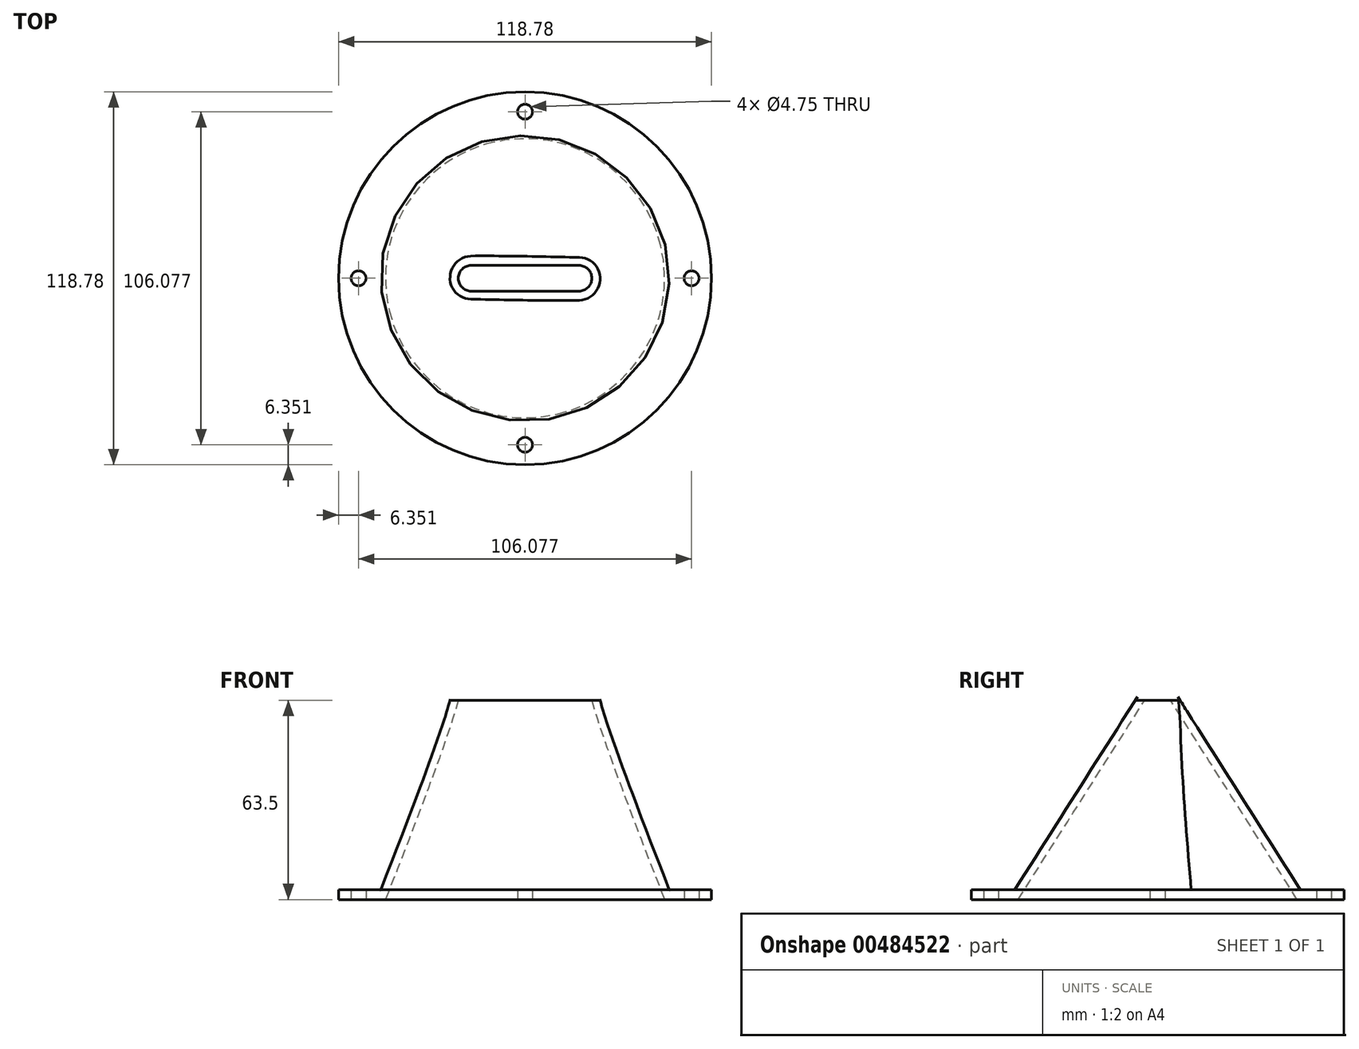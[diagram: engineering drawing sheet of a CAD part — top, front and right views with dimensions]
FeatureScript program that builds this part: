
annotation { "Feature Type Name" : "Feature", "Feature Type Description" : "" }
export const myFeature = defineFeature(function(context is Context, id is Id, definition is map)
    precondition{}
    {
        {
            var Q0;
            Q0=qCreatedBy(makeId("Top.planeOp"),FACE);
            var sketch = newSketch(context, id + "F0", { "sketchPlane" : qUnion([Q0])});
            skCircle(sketch, "E0", {"center": v(0, 0) * mm, "radius": 44.45 * mm});
            skSolve(sketch);
        }
        {
            var Q0;
            Q0=qCreatedBy(makeId("Top.planeOp"),FACE);
            cPlane(context, id + "F1", {"entities" : qUnion([Q0]), "cplaneType" : CPlaneType.OFFSET, "offset" : 63.5 * mm, "width" : 152.4 * mm, "height" : 152.4 * mm});
        }
        {
            var Q0;
            Q0=qCreatedBy(id+"F1.planeOp",FACE);
            var sketch = newSketch(context, id + "F2", { "sketchPlane" : qUnion([Q0])});
            skLineSegment(sketch, "E1.bottom", {"start": v(17.17, 4.1) * mm, "end": v(-17.17, 4.1) * mm});
            skLineSegment(sketch, "E1.top", {"start": v(17.17, -4.1) * mm, "end": v(-17.17, -4.1) * mm});
            skPoint(sketch, "E1.middle", {"position": v(0, 0) * mm});
            skArc(sketch, "E2", {"start": v(-17.17, 4.1) * mm, "mid": v(-21.28, 0) * mm, "end": v(-17.17, -4.1) * mm});
            skArc(sketch, "E3", {"start": v(17.17, -4.1) * mm, "mid": v(21.28, 0) * mm, "end": v(17.17, 4.1) * mm});
            skSolve(sketch);
        }
        {
            var Q0;
            Q0=makeQuery(id+"F0.imprint","IMPRINT",FACE,{"disambiguationData":[TD([[makeQuery(id+"F0.imprint","IMPRINT",EDGE,{"derivedFrom":sQuery(id+"F0.wireOp",EDGE,"E0")}),1.0]])]});
            var Q1;
            Q1=makeQuery(id+"F2.imprint","IMPRINT",FACE,{"disambiguationData":[TD([[makeQuery(id+"F2.imprint","IMPRINT",EDGE,{"derivedFrom":sQuery(id+"F2.wireOp",EDGE,"E1.bottom")}),1.0]])]});
            loft(context, id + "F3", {"sheetProfilesArray" : [{ "sheetProfileEntities" : qUnion([Q0]) }, { "sheetProfileEntities" : qUnion([Q1]) }]});
        }
        {
            var Q0;
            Q0=makeQuery(id+"F3.opLoft","CAP_FACE",FACE,{"disambiguationData":[OSD([makeQuery(id+"F0.imprint","IMPRINT",FACE,{"disambiguationData":[TD([[makeQuery(id+"F0.imprint","IMPRINT",EDGE,{"derivedFrom":sQuery(id+"F0.wireOp",EDGE,"E0")}),1.0]])]})])],"isStart":true});
            var Q1;
            Q1=makeQuery(id+"F3.opLoft","CAP_FACE",FACE,{"disambiguationData":[OSD([makeQuery(id+"F2.imprint","IMPRINT",FACE,{"disambiguationData":[TD([[makeQuery(id+"F2.imprint","IMPRINT",EDGE,{"derivedFrom":sQuery(id+"F2.wireOp",EDGE,"E1.bottom")}),1.0]])]})])],"isStart":true});
            shell(context, id + "F4", {"entities" : qUnion([Q0, Q1]), "thickness" : 2.54 * mm, "oppositeDirection" : true});
        }
        {
            var Q0;
            Q0=qCreatedBy(makeId("Top.planeOp"),FACE);
            var sketch = newSketch(context, id + "F5", { "sketchPlane" : qUnion([Q0])});
            skFitSpline(sketch, "E4.0", {"points": [v(-43.23, -10.34) * mm, v(-42.55, -13.18) * mm, v(-41.6, -15.92) * mm, v(-40.38, -18.57) * mm, v(-39.16, -21.23) * mm, v(-37.7, -23.73) * mm, v(-35.98, -26.1) * mm, v(-34.27, -28.46) * mm, v(-32.34, -30.63) * mm, v(-30.2, -32.61) * mm, v(-28.06, -34.6) * mm, v(-25.75, -36.35) * mm, v(-23.26, -37.88) * mm, v(-20.77, -39.4) * mm, v(-18.16, -40.68) * mm, v(-15.42, -41.69) * mm, v(-12.68, -42.7) * mm, v(-9.87, -43.44) * mm, v(-7, -43.9) * mm, v(-4.11, -44.36) * mm, v(-1.21, -44.53) * mm, v(1.7, -44.42) * mm, v(4.62, -44.3) * mm, v(7.5, -43.9) * mm, v(10.34, -43.23) * mm]});
            skFitSpline(sketch, "E5.0", {"points": [v(-10.34, 43.23) * mm, v(-13.18, 42.55) * mm, v(-15.92, 41.6) * mm, v(-18.57, 40.38) * mm, v(-21.23, 39.16) * mm, v(-23.73, 37.7) * mm, v(-26.1, 35.98) * mm, v(-28.46, 34.27) * mm, v(-30.63, 32.34) * mm, v(-32.61, 30.2) * mm, v(-34.6, 28.06) * mm, v(-36.35, 25.75) * mm, v(-37.88, 23.26) * mm, v(-39.4, 20.77) * mm, v(-40.68, 18.16) * mm, v(-41.69, 15.42) * mm, v(-42.7, 12.68) * mm, v(-43.44, 9.87) * mm, v(-43.9, 7) * mm, v(-44.36, 4.11) * mm, v(-44.53, 1.21) * mm, v(-44.42, -1.7) * mm, v(-44.3, -4.62) * mm, v(-43.9, -7.5) * mm, v(-43.23, -10.34) * mm]});
            skFitSpline(sketch, "E6.0", {"points": [v(43.23, 10.34) * mm, v(42.55, 13.18) * mm, v(41.6, 15.92) * mm, v(40.38, 18.57) * mm, v(39.16, 21.23) * mm, v(37.7, 23.73) * mm, v(35.98, 26.1) * mm, v(34.27, 28.46) * mm, v(32.34, 30.63) * mm, v(30.2, 32.61) * mm, v(28.06, 34.6) * mm, v(25.75, 36.35) * mm, v(23.26, 37.88) * mm, v(20.77, 39.4) * mm, v(18.16, 40.68) * mm, v(15.42, 41.69) * mm, v(12.68, 42.7) * mm, v(9.87, 43.44) * mm, v(7, 43.9) * mm, v(4.11, 44.36) * mm, v(1.21, 44.53) * mm, v(-1.7, 44.42) * mm, v(-4.62, 44.3) * mm, v(-7.5, 43.9) * mm, v(-10.34, 43.23) * mm]});
            skFitSpline(sketch, "E7.0", {"points": [v(10.34, -43.23) * mm, v(13.18, -42.55) * mm, v(15.92, -41.6) * mm, v(18.57, -40.38) * mm, v(21.23, -39.16) * mm, v(23.73, -37.7) * mm, v(26.1, -35.98) * mm, v(28.46, -34.27) * mm, v(30.63, -32.34) * mm, v(32.61, -30.2) * mm, v(34.6, -28.06) * mm, v(36.35, -25.75) * mm, v(37.88, -23.26) * mm, v(39.4, -20.77) * mm, v(40.68, -18.16) * mm, v(41.69, -15.42) * mm, v(42.7, -12.68) * mm, v(43.44, -9.87) * mm, v(43.9, -7) * mm, v(44.36, -4.11) * mm, v(44.53, -1.21) * mm, v(44.42, 1.7) * mm, v(44.3, 4.62) * mm, v(43.9, 7.5) * mm, v(43.23, 10.34) * mm]});
            skCircle(sketch, "E8", {"center": v(0, 0) * mm, "radius": 59.39 * mm});
            skSolve(sketch);
        }
        {
            var Q0;
            Q0=makeQuery(id+"F5.imprint","IMPRINT",FACE,{"disambiguationData":[TD([[makeQuery(id+"F5.imprint","IMPRINT",EDGE,{"derivedFrom":sQuery(id+"F5.wireOp",EDGE,"E4.0")}),-1.0]])]});
            extrude(context, id + "F6", {"entities" : qUnion([Q0]), "operationType" : NewBodyOperationType.ADD, "depth" : 3.17 * mm});
        }
        {
            var Q0;
            Q0=qCreatedBy(makeId("Top.planeOp"),FACE);
            var sketch = newSketch(context, id + "F7", { "sketchPlane" : qUnion([Q0])});
            skLineSegment(sketch, "E9", {"start": v(0, 0) * mm, "end": v(0, -53.04) * mm, "construction": true});
            skLineSegment(sketch, "E10", {"start": v(0, 0) * mm, "end": v(0, 53.04) * mm, "construction": true});
            skLineSegment(sketch, "E11", {"start": v(0, 0) * mm, "end": v(53.04, 0) * mm, "construction": true});
            skLineSegment(sketch, "E12", {"start": v(0, 0) * mm, "end": v(-53.04, 0) * mm, "construction": true});
            skCircle(sketch, "E13.0", {"center": v(0, 0) * mm, "radius": 53.04 * mm, "construction": true});
            skSolve(sketch);
        }
        {
            var Q0;
            Q0=sQuery(id+"F7.wireOp",VERTEX,"E9.end");
            var Q1;
            Q1=sQuery(id+"F7.wireOp",VERTEX,"E12.end");
            var Q2;
            Q2=sQuery(id+"F7.wireOp",VERTEX,"E11.end");
            var Q3;
            Q3=sQuery(id+"F7.wireOp",VERTEX,"E10.end");
            var Q4;
            Q4=makeQuery(id+"F3.opLoft","SWEPT_BODY",BODY,{"disambiguationData":[OSD([makeQuery(id+"F0.imprint","IMPRINT",FACE,{"disambiguationData":[TD([[makeQuery(id+"F0.imprint","IMPRINT",EDGE,{"derivedFrom":sQuery(id+"F0.wireOp",EDGE,"E0")}),1.0]])]}),makeQuery(id+"F2.imprint","IMPRINT",FACE,{"disambiguationData":[TD([[makeQuery(id+"F2.imprint","IMPRINT",EDGE,{"derivedFrom":sQuery(id+"F2.wireOp",EDGE,"E1.bottom")}),1.0]])]})])]});
            hole(context, id + "F8", {"style" : HoleStyle.SIMPLE, "endStyle" : HoleEndStyle.THROUGH, "oppositeDirection" : true, "holeDiameter" : 4.75 * mm, "isTappedThrough" : true, "tappedDepth" : 12.7 * mm, "tapClearance" : 3, "startFromSketch" : true, "locations" : qUnion([Q0, Q1, Q2, Q3]), "scope" : qUnion([Q4])});
        }
    });
